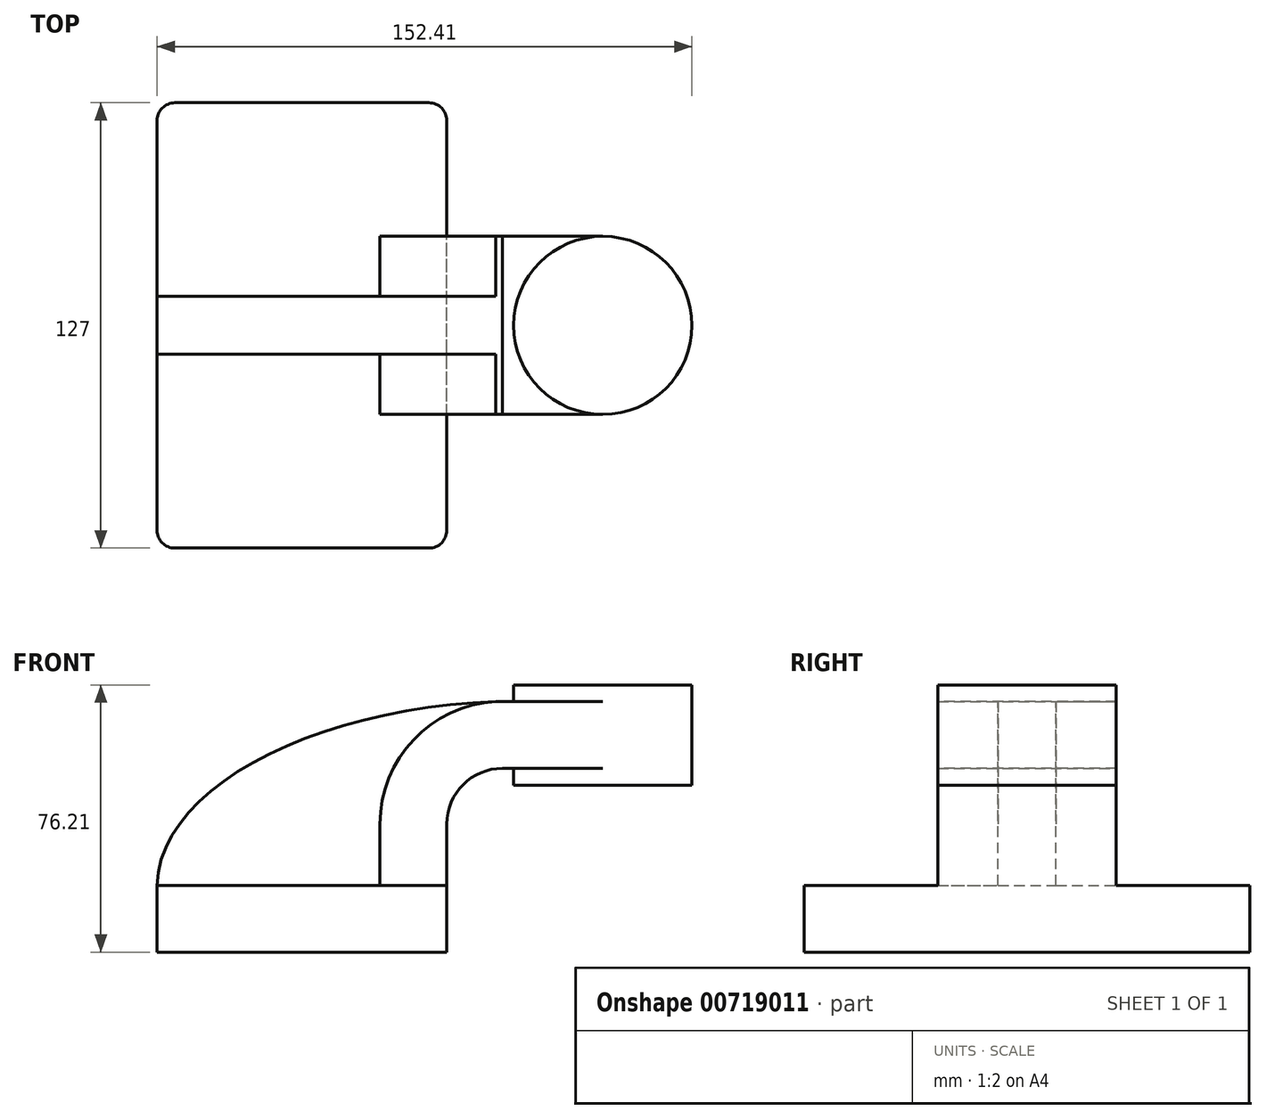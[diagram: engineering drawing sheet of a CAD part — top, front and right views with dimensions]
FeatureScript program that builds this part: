
annotation { "Feature Type Name" : "Feature", "Feature Type Description" : "" }
export const myFeature = defineFeature(function(context is Context, id is Id, definition is map)
    precondition{}
    {
        {
            var Q0;
            Q0=qCreatedBy(makeId("Front.planeOp"),FACE);
            var sketch = newSketch(context, id + "F0", { "sketchPlane" : qUnion([Q0])});
            skLineSegment(sketch, "E0.bottom", {"start": v(41.28, -9.52) * mm, "end": v(-41.27, -9.52) * mm});
            skLineSegment(sketch, "E0.top", {"start": v(41.27, 9.53) * mm, "end": v(-41.28, 9.53) * mm});
            skLineSegment(sketch, "E0.left", {"start": v(41.28, -9.52) * mm, "end": v(41.28, 9.53) * mm});
            skLineSegment(sketch, "E0.right", {"start": v(-41.27, -9.52) * mm, "end": v(-41.28, 9.52) * mm});
            skPoint(sketch, "E0.middle", {"position": v(0, 0) * mm});
            skLineSegment(sketch, "E1.bottom", {"start": v(111.13, 38.1) * mm, "end": v(60.33, 38.1) * mm});
            skLineSegment(sketch, "E1.top", {"start": v(111.13, 66.68) * mm, "end": v(60.33, 66.68) * mm});
            skLineSegment(sketch, "E1.left", {"start": v(111.13, 38.1) * mm, "end": v(111.13, 66.68) * mm});
            skLineSegment(sketch, "E1.right", {"start": v(60.33, 38.1) * mm, "end": v(60.33, 66.68) * mm});
            skPoint(sketch, "E1.middle", {"position": v(85.73, 52.39) * mm});
            skLineSegment(sketch, "E2", {"start": v(41.27, 9.53) * mm, "end": v(41.27, 27) * mm});
            skArc(sketch, "E3", {"start": v(41.28, 27) * mm, "mid": v(45.92, 38.23) * mm, "end": v(57.15, 42.88) * mm});
            skLineSegment(sketch, "E4", {"start": v(57.15, 42.88) * mm, "end": v(85.73, 42.88) * mm});
            skLineSegment(sketch, "E5.0", {"start": v(57.15, 61.93) * mm, "end": v(85.73, 61.93) * mm});
            skArc(sketch, "E5.1", {"start": v(22.23, 27) * mm, "mid": v(32.45, 51.7) * mm, "end": v(57.15, 61.93) * mm});
            skLineSegment(sketch, "E5.2", {"start": v(22.23, 9.53) * mm, "end": v(22.23, 27) * mm});
            skLineSegment(sketch, "E6", {"start": v(85.73, 66.68) * mm, "end": v(85.73, 38.1) * mm});
            skFitSpline(sketch, "E7", {"points": [v(-41.28, 9.53) * mm, v(57.15, 61.93) * mm], "startDerivative": vector(2.1, 86.27) * mm, "endDerivative": vector(153.3, 3.37) * mm});
            skSolve(sketch);
        }
        {
            var Q0;
            Q0=makeQuery(id+"F0.imprint","IMPRINT",FACE,{"disambiguationData":[TD([[makeQuery(id+"F0.imprint","IMPRINT",EDGE,{"derivedFrom":sQuery(id+"F0.wireOp",EDGE,"E0.bottom")}),-1.0]])]});
            extrude(context, id + "F1", {"entities" : qUnion([Q0]), "endBound" : BoundingType.SYMMETRIC, "depth" : 127 * mm, "offsetDistance" : 25.4 * mm});
        }
        {
            var Q0;
            {var subQ1=sQuery(id+"F0.wireOp",EDGE,"E2");Q0=makeQuery(id+"F0.imprint","IMPRINT",FACE,{"disambiguationData":[TD([[makeQuery(id+"F0.imprint","IMPRINT",EDGE,{"derivedFrom":subQ1}),1.0]])]});}
            var Q1;
            {var subQ0=sQuery(id+"F0.wireOp",EDGE,"E4");var subQ1=sQuery(id+"F0.wireOp",EDGE,"E1.right");var subQ2=makeQuery(id+"F0.imprint","INTERSECT",VERTEX,{"derivedFrom":[subQ1,subQ0]});Q1=makeQuery(id+"F0.imprint","IMPRINT",FACE,{"disambiguationData":[TD([[makeQuery(id+"F0.imprint","IMPRINT",EDGE,{"disambiguationData":[TD([[subQ2,-1.0]])],"derivedFrom":subQ1}),-1.0]])]});}
            extrude(context, id + "F2", {"entities" : qUnion([Q0, Q1]), "operationType" : NewBodyOperationType.ADD, "endBound" : BoundingType.SYMMETRIC, "depth" : 50.8 * mm, "offsetDistance" : 25.4 * mm});
        }
        {
            var Q0;
            {var subQ3=sQuery(id+"F0.wireOp",EDGE,"E5.2");Q0=makeQuery(id+"F0.imprint","IMPRINT",FACE,{"disambiguationData":[TD([[makeQuery(id+"F0.imprint","IMPRINT",EDGE,{"derivedFrom":subQ3}),1.0]])]});}
            extrude(context, id + "F3", {"entities" : qUnion([Q0]), "operationType" : NewBodyOperationType.ADD, "endBound" : BoundingType.SYMMETRIC, "depth" : 16.5 * mm, "offsetDistance" : 25.4 * mm});
        }
        {
            var Q0;
            {var subQ0=sQuery(id+"F0.wireOp",EDGE,"E1.left");Q0=makeQuery(id+"F0.imprint","IMPRINT",FACE,{"disambiguationData":[TD([[makeQuery(id+"F0.imprint","IMPRINT",EDGE,{"derivedFrom":subQ0}),1.0]])]});}
            var Q1;
            Q1=sQuery(id+"F0.wireOp",EDGE,"E6");
            revolve(context, id + "F4", {"operationType" : NewBodyOperationType.ADD, "surfaceOperationType" : NewSurfaceOperationType.NEW, "entities" : qUnion([Q0]), "axis" : qUnion([Q1]), "revolveType" : RevolveType.FULL});
        }
        {
            var Q0;
            Q0=makeQuery(id+"F1.opExtrude","CAP_EDGE",EDGE,{"disambiguationData":[OSD([sQuery(id+"F0.wireOp",EDGE,"E0.left")])],"isStart":true});
            var Q1;
            Q1=makeQuery(id+"F1.opExtrude","CAP_EDGE",EDGE,{"disambiguationData":[OSD([sQuery(id+"F0.wireOp",EDGE,"E0.right")])],"isStart":true});
            var Q2;
            Q2=makeQuery(id+"F1.opExtrude","CAP_EDGE",EDGE,{"disambiguationData":[OSD([sQuery(id+"F0.wireOp",EDGE,"E0.left")])],"isStart":false});
            var Q3;
            Q3=makeQuery(id+"F1.opExtrude","CAP_EDGE",EDGE,{"disambiguationData":[OSD([sQuery(id+"F0.wireOp",EDGE,"E0.right")])],"isStart":false});
            fillet(context, id + "F5", {"entities" : qUnion([Q0, Q1, Q2, Q3]), "radius" : 5.08 * mm, "tangentPropagation" : true, "allowEdgeOverflow" : false});
        }
    });
